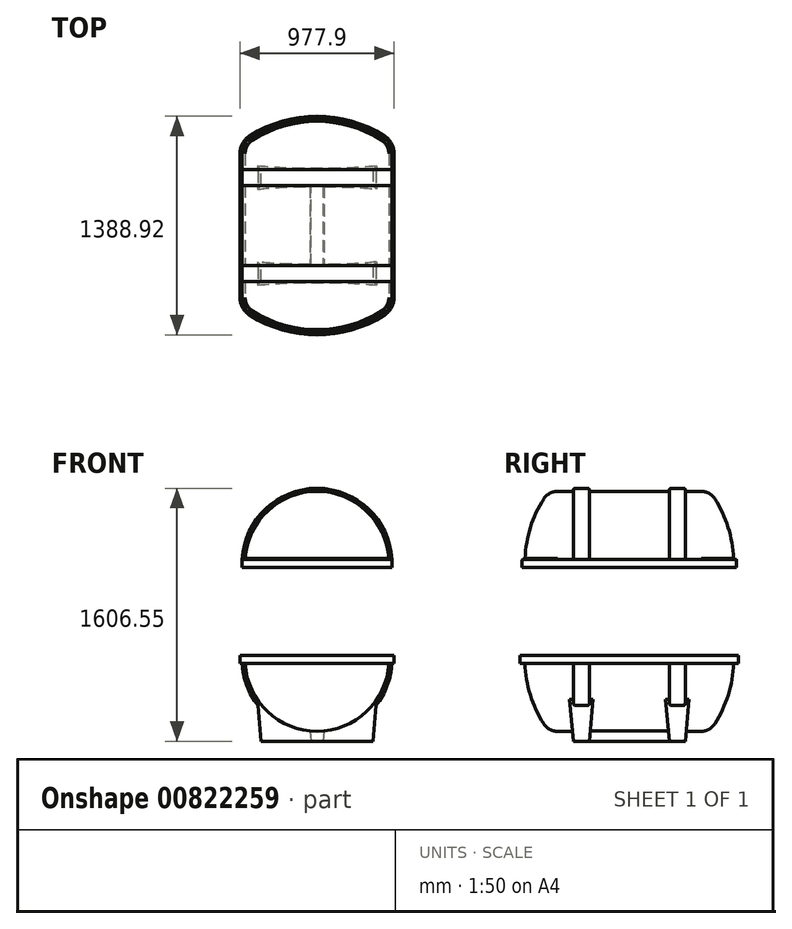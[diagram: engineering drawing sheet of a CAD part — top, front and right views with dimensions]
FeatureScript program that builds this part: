
annotation { "Feature Type Name" : "Feature", "Feature Type Description" : "" }
export const myFeature = defineFeature(function(context is Context, id is Id, definition is map)
    precondition{}
    {
        {
            var Q0;
            Q0=qCreatedBy(makeId("Right.planeOp"),FACE);
            var sketch = newSketch(context, id + "F0", { "sketchPlane" : qUnion([Q0])});
            skLineSegment(sketch, "E0", {"start": v(0, 0) * mm, "end": v(0, 429.3) * mm, "construction": true});
            skLineSegment(sketch, "E1", {"start": v(0, 0) * mm, "end": v(-983.56, 0) * mm, "construction": true});
            skLineSegment(sketch, "E2", {"start": v(0, 457.2) * mm, "end": v(-457.2, 457.2) * mm});
            skArc(sketch, "E3", {"start": v(-457.2, 457.2) * mm, "mid": v(-506, 444.7) * mm, "end": v(-542.81, 410.3) * mm});
            skArc(sketch, "E4", {"start": v(-542.81, 410.3) * mm, "mid": v(-632.12, 213.73) * mm, "end": v(-662.71, 0) * mm});
            skLineSegment(sketch, "E5", {"start": v(-662.71, 0) * mm, "end": v(-662.71, 430.73) * mm, "construction": true});
            skLineSegment(sketch, "E6.MirrorCS", {"start": v(0, 457.2) * mm, "end": v(457.2, 457.2) * mm});
            skArc(sketch, "E7.MirrorCS", {"start": v(457.2, 457.2) * mm, "mid": v(506, 444.7) * mm, "end": v(542.81, 410.3) * mm});
            skArc(sketch, "E8.MirrorCS", {"start": v(542.81, 410.3) * mm, "mid": v(632.12, 213.73) * mm, "end": v(662.71, 0) * mm});
            skLineSegment(sketch, "E9", {"start": v(-662.71, 0) * mm, "end": v(662.71, 0) * mm});
            skLineSegment(sketch, "E10.bottom", {"start": v(254, 457.2) * mm, "end": v(355.6, 457.2) * mm});
            skLineSegment(sketch, "E10.top", {"start": v(263.53, 476.25) * mm, "end": v(346.08, 476.25) * mm});
            skLineSegment(sketch, "E10.left", {"start": v(254, 457.2) * mm, "end": v(254, 466.73) * mm});
            skLineSegment(sketch, "E10.right", {"start": v(355.6, 457.2) * mm, "end": v(355.6, 466.73) * mm});
            skPoint(sketch, "E11.visualSharp", {"position": v(254, 476.25) * mm});
            skArc(sketch, "E11.filletArc", {"start": v(263.53, 476.25) * mm, "mid": v(256.79, 473.46) * mm, "end": v(254, 466.73) * mm});
            skPoint(sketch, "E12.visualSharp", {"position": v(355.6, 476.25) * mm});
            skArc(sketch, "E12.filletArc", {"start": v(355.6, 466.73) * mm, "mid": v(352.81, 473.46) * mm, "end": v(346.08, 476.25) * mm});
            skLineSegment(sketch, "E13.MirrorCS", {"start": v(-355.6, 457.2) * mm, "end": v(-355.6, 466.73) * mm});
            skArc(sketch, "E14.MirrorCS", {"start": v(-263.53, 476.25) * mm, "mid": v(-256.79, 473.46) * mm, "end": v(-254, 466.73) * mm});
            skLineSegment(sketch, "E15.MirrorCS", {"start": v(-254, 457.2) * mm, "end": v(-254, 466.73) * mm});
            skArc(sketch, "E16.MirrorCS", {"start": v(-355.6, 466.73) * mm, "mid": v(-352.81, 473.46) * mm, "end": v(-346.08, 476.25) * mm});
            skPoint(sketch, "E17.MirrorP", {"position": v(-254, 476.25) * mm});
            skLineSegment(sketch, "E18.MirrorCS", {"start": v(-263.53, 476.25) * mm, "end": v(-346.08, 476.25) * mm});
            skLineSegment(sketch, "E19.MirrorCS", {"start": v(-254, 457.2) * mm, "end": v(-355.6, 457.2) * mm});
            skPoint(sketch, "E20.MirrorP", {"position": v(-355.6, 476.25) * mm});
            skSolve(sketch);
        }
        {
            var Q0;
            {var subQ8=sQuery(id+"F0.wireOp",EDGE,"E3");Q0=makeQuery(id+"F0.imprint","IMPRINT",FACE,{"disambiguationData":[TD([[makeQuery(id+"F0.imprint","IMPRINT",EDGE,{"derivedFrom":subQ8}),1.0]])]});}
            var Q1;
            {var subQ1=sQuery(id+"F0.wireOp",EDGE,"E13.MirrorCS");Q1=makeQuery(id+"F0.imprint","IMPRINT",FACE,{"disambiguationData":[TD([[makeQuery(id+"F0.imprint","IMPRINT",EDGE,{"derivedFrom":subQ1}),-1.0]])]});}
            var Q2;
            Q2=makeQuery(id+"F0.imprint","IMPRINT",FACE,{"disambiguationData":[TD([[makeQuery(id+"F0.imprint","IMPRINT",EDGE,{"derivedFrom":sQuery(id+"F0.wireOp",EDGE,"E10.top")}),-1.0]])]});
            var Q3;
            Q3=sQuery(id+"F0.wireOp",EDGE,"E9");
            revolve(context, id + "F1", {"surfaceOperationType" : NewSurfaceOperationType.NEW, "entities" : qUnion([Q0, Q1, Q2]), "axis" : qUnion([Q3]), "revolveType" : RevolveType.SYMMETRIC, "angle" : 180 * degree});
        }
        {
            var Q0;
            Q0=qCreatedBy(makeId("Top.planeOp"),FACE);
            var sketch = newSketch(context, id + "F2", { "sketchPlane" : qUnion([Q0])});
            skArc(sketch, "E21.0", {"start": v(410.3, 542.81) * mm, "mid": v(0, 662.71) * mm, "end": v(-410.3, 542.81) * mm});
            skLineSegment(sketch, "E22.0", {"start": v(-488.95, -457.2) * mm, "end": v(-488.95, 457.2) * mm});
            skArc(sketch, "E22.1", {"start": v(-488.95, -457.2) * mm, "mid": v(-472.56, -521.26) * mm, "end": v(-427.4, -569.57) * mm});
            skArc(sketch, "E22.2", {"start": v(-488.95, 457.2) * mm, "mid": v(-472.56, 521.26) * mm, "end": v(-427.4, 569.57) * mm});
            skArc(sketch, "E22.3", {"start": v(427.4, -569.57) * mm, "mid": v(0, -694.46) * mm, "end": v(-427.4, -569.57) * mm});
            skArc(sketch, "E22.4", {"start": v(427.4, 569.57) * mm, "mid": v(0, 694.46) * mm, "end": v(-427.4, 569.57) * mm});
            skArc(sketch, "E22.5", {"start": v(488.95, 457.2) * mm, "mid": v(472.56, 521.26) * mm, "end": v(427.4, 569.57) * mm});
            skLineSegment(sketch, "E22.6", {"start": v(488.95, -457.2) * mm, "end": v(488.95, 457.2) * mm});
            skArc(sketch, "E22.7", {"start": v(488.95, -457.2) * mm, "mid": v(472.56, -521.26) * mm, "end": v(427.4, -569.57) * mm});
            skSolve(sketch);
        }
        {
            var Q0;
            Q0=makeQuery(id+"F2.imprint","IMPRINT",FACE,{"disambiguationData":[TD([[makeQuery(id+"F2.imprint","IMPRINT",EDGE,{"derivedFrom":sQuery(id+"F2.wireOp",EDGE,"E22.0")}),-1.0]])]});
            extrude(context, id + "F3", {"entities" : qUnion([Q0]), "operationType" : NewBodyOperationType.ADD, "endBound" : BoundingType.SYMMETRIC, "depth" : 50.8 * mm, "offsetDistance" : 25.4 * mm});
        }
        {
            var Q0;
            Q0=qCreatedBy(makeId("Top.planeOp"),FACE);
            cPlane(context, id + "F4", {"entities" : qUnion([Q0]), "cplaneType" : CPlaneType.OFFSET, "offset" : 304.8 * mm, "oppositeDirection" : true, "width" : 152.4 * mm, "height" : 152.4 * mm});
        }
        {
            var Q0;
            Q0=makeQuery(id+"F1.opRevolve","SWEPT_BODY",BODY,{"disambiguationData":[OSD([sQuery(id+"F0.wireOp",EDGE,"E2"),sQuery(id+"F0.wireOp",EDGE,"E3"),sQuery(id+"F0.wireOp",EDGE,"E4"),sQuery(id+"F0.wireOp",EDGE,"E6.MirrorCS"),sQuery(id+"F0.wireOp",EDGE,"E7.MirrorCS"),sQuery(id+"F0.wireOp",EDGE,"E8.MirrorCS"),sQuery(id+"F0.wireOp",EDGE,"E9"),sQuery(id+"F0.wireOp",EDGE,"E10.top"),sQuery(id+"F0.wireOp",EDGE,"E10.left"),sQuery(id+"F0.wireOp",EDGE,"E10.right"),sQuery(id+"F0.wireOp",EDGE,"E11.filletArc"),sQuery(id+"F0.wireOp",EDGE,"E12.filletArc"),sQuery(id+"F0.wireOp",EDGE,"E13.MirrorCS"),sQuery(id+"F0.wireOp",EDGE,"E14.MirrorCS"),sQuery(id+"F0.wireOp",EDGE,"E15.MirrorCS"),sQuery(id+"F0.wireOp",EDGE,"E16.MirrorCS"),sQuery(id+"F0.wireOp",EDGE,"E18.MirrorCS")])]});
            var Q1;
            Q1=qCreatedBy(id+"F4.planeOp",FACE);
            mirror(context, id + "F5", {"entities" : qUnion([Q0]), "mirrorPlane" : qUnion([Q1])});
        }
        {
            var Q0;
            Q0=makeQuery(id+"F3.opExtrude","CAP_FACE",FACE,{"disambiguationData":[OSD([sQuery(id+"F2.wireOp",EDGE,"E22.0"),sQuery(id+"F2.wireOp",EDGE,"E22.1"),sQuery(id+"F2.wireOp",EDGE,"E22.2"),sQuery(id+"F2.wireOp",EDGE,"E22.3"),sQuery(id+"F2.wireOp",EDGE,"E22.4"),sQuery(id+"F2.wireOp",EDGE,"E22.5"),sQuery(id+"F2.wireOp",EDGE,"E22.6"),sQuery(id+"F2.wireOp",EDGE,"E22.7")])],"isStart":true});
            var sketch = newSketch(context, id + "F6", { "sketchPlane" : qUnion([Q0])});
            skLineSegment(sketch, "E23.0", {"start": v(476.25, -457.2) * mm, "end": v(476.25, 457.2) * mm});
            skArc(sketch, "E23.1", {"start": v(420.57, -558.87) * mm, "mid": v(461.42, -515.16) * mm, "end": v(476.25, -457.2) * mm});
            skArc(sketch, "E23.2", {"start": v(476.25, 457.2) * mm, "mid": v(461.42, 515.16) * mm, "end": v(420.57, 558.87) * mm});
            skArc(sketch, "E23.3", {"start": v(-420.57, -558.87) * mm, "mid": v(0, -681.76) * mm, "end": v(420.57, -558.87) * mm});
            skArc(sketch, "E23.4", {"start": v(420.57, 558.87) * mm, "mid": v(0, 681.76) * mm, "end": v(-420.57, 558.87) * mm});
            skArc(sketch, "E23.5", {"start": v(-420.57, 558.87) * mm, "mid": v(-461.42, 515.16) * mm, "end": v(-476.25, 457.2) * mm});
            skLineSegment(sketch, "E23.6", {"start": v(-476.25, 457.2) * mm, "end": v(-476.25, -457.2) * mm});
            skArc(sketch, "E23.7", {"start": v(-476.25, -457.2) * mm, "mid": v(-461.42, -515.16) * mm, "end": v(-420.57, -558.87) * mm});
            skSolve(sketch);
        }
        {
            var Q0;
            Q0=makeQuery(id+"F6.imprint","IMPRINT",FACE,{"disambiguationData":[TD([[makeQuery(id+"F6.imprint","IMPRINT",EDGE,{"derivedFrom":sQuery(id+"F6.wireOp",EDGE,"E23.0")}),-1.0]])]});
            extrude(context, id + "F7", {"entities" : qUnion([Q0]), "operationType" : NewBodyOperationType.REMOVE, "endBound" : BoundingType.THROUGH_ALL, "oppositeDirection" : true, "depth" : 25.4 * mm, "offsetDistance" : 25.4 * mm});
        }
        {
            var Q0;
            Q0=makeQuery(id+"F5.opPattern","COPY",FACE,{"derivedFrom":makeQuery(id+"F3.opExtrude","CAP_FACE",FACE,{"disambiguationData":[OSD([sQuery(id+"F2.wireOp",EDGE,"E22.0"),sQuery(id+"F2.wireOp",EDGE,"E22.1"),sQuery(id+"F2.wireOp",EDGE,"E22.2"),sQuery(id+"F2.wireOp",EDGE,"E22.3"),sQuery(id+"F2.wireOp",EDGE,"E22.4"),sQuery(id+"F2.wireOp",EDGE,"E22.5"),sQuery(id+"F2.wireOp",EDGE,"E22.6"),sQuery(id+"F2.wireOp",EDGE,"E22.7")])],"isStart":true}),"instanceName":"1"});
            cPlane(context, id + "F8", {"entities" : qUnion([Q0]), "cplaneType" : CPlaneType.OFFSET, "offset" : 546.1 * mm, "oppositeDirection" : true, "width" : 152.4 * mm, "height" : 152.4 * mm});
        }
        {
            var Q0;
            Q0=qCreatedBy(id+"F8.planeOp",FACE);
            var sketch = newSketch(context, id + "F9", { "sketchPlane" : qUnion([Q0])});
            skLineSegment(sketch, "E24", {"start": v(0, 0) * mm, "end": v(38.1, 0) * mm});
            skLineSegment(sketch, "E25", {"start": v(38.1, 0) * mm, "end": v(38.1, -254) * mm});
            skLineSegment(sketch, "E26", {"start": v(38.1, -254) * mm, "end": v(355.6, -254) * mm});
            skLineSegment(sketch, "E27", {"start": v(355.6, -254) * mm, "end": v(355.6, -355.6) * mm});
            skLineSegment(sketch, "E28", {"start": v(355.6, -355.6) * mm, "end": v(0, -355.6) * mm});
            skLineSegment(sketch, "E29", {"start": v(0, -355.6) * mm, "end": v(0, 0) * mm, "construction": true});
            skLineSegment(sketch, "E30", {"start": v(414.4, 0) * mm, "end": v(0, 0) * mm, "construction": true});
            skLineSegment(sketch, "E31.MirrorCS", {"start": v(0, 0) * mm, "end": v(-38.1, 0) * mm});
            skLineSegment(sketch, "E32.MirrorCS", {"start": v(-38.1, 0) * mm, "end": v(-38.1, -254) * mm});
            skLineSegment(sketch, "E33.MirrorCS", {"start": v(-38.1, -254) * mm, "end": v(-355.6, -254) * mm});
            skLineSegment(sketch, "E34.MirrorCS", {"start": v(-355.6, -254) * mm, "end": v(-355.6, -355.6) * mm});
            skLineSegment(sketch, "E35.MirrorCS", {"start": v(-355.6, -355.6) * mm, "end": v(0, -355.6) * mm});
            skLineSegment(sketch, "E36.MirrorCS", {"start": v(38.1, 0) * mm, "end": v(38.1, 254) * mm});
            skLineSegment(sketch, "E37.MirrorCS", {"start": v(38.1, 254) * mm, "end": v(355.6, 254) * mm});
            skLineSegment(sketch, "E38.MirrorCS", {"start": v(355.6, 355.6) * mm, "end": v(0, 355.6) * mm});
            skLineSegment(sketch, "E39.MirrorCS", {"start": v(355.6, 254) * mm, "end": v(355.6, 355.6) * mm});
            skLineSegment(sketch, "E40.MirrorCS", {"start": v(-355.6, 254) * mm, "end": v(-355.6, 355.6) * mm});
            skLineSegment(sketch, "E41.MirrorCS", {"start": v(-355.6, 355.6) * mm, "end": v(0, 355.6) * mm});
            skLineSegment(sketch, "E42.MirrorCS", {"start": v(-38.1, 254) * mm, "end": v(-355.6, 254) * mm});
            skLineSegment(sketch, "E43.MirrorCS", {"start": v(-38.1, 0) * mm, "end": v(-38.1, 254) * mm});
            skSolve(sketch);
        }
        {
            var Q0;
            Q0=makeQuery(id+"F9.imprint","IMPRINT",FACE,{"disambiguationData":[TD([[makeQuery(id+"F9.imprint","IMPRINT",EDGE,{"derivedFrom":sQuery(id+"F9.wireOp",EDGE,"E24")}),-1.0]])]});
            var Q1;
            Q1=makeQuery(id+"F9.imprint","IMPRINT",FACE,{"disambiguationData":[TD([[makeQuery(id+"F9.imprint","IMPRINT",EDGE,{"derivedFrom":sQuery(id+"F9.wireOp",EDGE,"E24")}),1.0]])]});
            var Q2;
            Q2=makeQuery(id+"F5.opPattern","COPY",FACE,{"derivedFrom":makeQuery(id+"F1.opRevolve","SWEPT_FACE",FACE,{"disambiguationData":[OSD([sQuery(id+"F0.wireOp",EDGE,"E2"),sQuery(id+"F0.wireOp",EDGE,"E6.MirrorCS")])]}),"instanceName":"1"});
            extrude(context, id + "F10", {"entities" : qUnion([Q0, Q1]), "operationType" : NewBodyOperationType.ADD, "endBound" : BoundingType.UP_TO_SURFACE, "depth" : 25.4 * mm, "endBoundEntityFace" : qUnion([Q2]), "offsetDistance" : 25.4 * mm, "hasDraft" : true, "draftAngle" : 5 * degree});
        }
        {
            var Q0;
            Q0=makeQuery(id+"F7.boolean.opBoolean","INTERSECT",EDGE,{"derivedFrom":[makeQuery(id+"F3.opExtrude","CAP_FACE",FACE,{"disambiguationData":[OSD([sQuery(id+"F2.wireOp",EDGE,"E22.0"),sQuery(id+"F2.wireOp",EDGE,"E22.1"),sQuery(id+"F2.wireOp",EDGE,"E22.2"),sQuery(id+"F2.wireOp",EDGE,"E22.3"),sQuery(id+"F2.wireOp",EDGE,"E22.4"),sQuery(id+"F2.wireOp",EDGE,"E22.5"),sQuery(id+"F2.wireOp",EDGE,"E22.6"),sQuery(id+"F2.wireOp",EDGE,"E22.7")])],"isStart":false}),makeQuery(id+"F7.opExtrude","SWEPT_FACE",FACE,{"disambiguationData":[OSD([sQuery(id+"F6.wireOp",EDGE,"E23.6")])]})]});
            var Q1;
            Q1=makeQuery(id+"F7.boolean.opBoolean","INTERSECT",EDGE,{"derivedFrom":[makeQuery(id+"F3.opExtrude","CAP_FACE",FACE,{"disambiguationData":[OSD([sQuery(id+"F2.wireOp",EDGE,"E22.0"),sQuery(id+"F2.wireOp",EDGE,"E22.1"),sQuery(id+"F2.wireOp",EDGE,"E22.2"),sQuery(id+"F2.wireOp",EDGE,"E22.3"),sQuery(id+"F2.wireOp",EDGE,"E22.4"),sQuery(id+"F2.wireOp",EDGE,"E22.5"),sQuery(id+"F2.wireOp",EDGE,"E22.6"),sQuery(id+"F2.wireOp",EDGE,"E22.7")])],"isStart":false}),makeQuery(id+"F7.opExtrude","SWEPT_FACE",FACE,{"disambiguationData":[OSD([sQuery(id+"F6.wireOp",EDGE,"E23.5")])]})]});
            var Q2;
            Q2=makeQuery(id+"F3.boolean.opBoolean","INTERSECT",EDGE,{"derivedFrom":[makeQuery(id+"F1.opRevolve","SWEPT_FACE",FACE,{"disambiguationData":[OSD([sQuery(id+"F0.wireOp",EDGE,"E4")])]}),makeQuery(id+"F3.opExtrude","CAP_FACE",FACE,{"disambiguationData":[OSD([sQuery(id+"F2.wireOp",EDGE,"E22.0"),sQuery(id+"F2.wireOp",EDGE,"E22.1"),sQuery(id+"F2.wireOp",EDGE,"E22.2"),sQuery(id+"F2.wireOp",EDGE,"E22.3"),sQuery(id+"F2.wireOp",EDGE,"E22.4"),sQuery(id+"F2.wireOp",EDGE,"E22.5"),sQuery(id+"F2.wireOp",EDGE,"E22.6"),sQuery(id+"F2.wireOp",EDGE,"E22.7")])],"isStart":false})]});
            var Q3;
            Q3=makeQuery(id+"F3.boolean.opBoolean","INTERSECT",EDGE,{"disambiguationData":[OD(0.0)],"derivedFrom":[makeQuery(id+"F1.opRevolve","SWEPT_FACE",FACE,{"disambiguationData":[OSD([sQuery(id+"F0.wireOp",EDGE,"E2"),sQuery(id+"F0.wireOp",EDGE,"E6.MirrorCS")])]}),makeQuery(id+"F3.opExtrude","CAP_FACE",FACE,{"disambiguationData":[OSD([sQuery(id+"F2.wireOp",EDGE,"E22.0"),sQuery(id+"F2.wireOp",EDGE,"E22.1"),sQuery(id+"F2.wireOp",EDGE,"E22.2"),sQuery(id+"F2.wireOp",EDGE,"E22.3"),sQuery(id+"F2.wireOp",EDGE,"E22.4"),sQuery(id+"F2.wireOp",EDGE,"E22.5"),sQuery(id+"F2.wireOp",EDGE,"E22.6"),sQuery(id+"F2.wireOp",EDGE,"E22.7")])],"isStart":false})]});
            var Q4;
            Q4=makeQuery(id+"F3.boolean.opBoolean","INTERSECT",EDGE,{"disambiguationData":[OD(0.0)],"derivedFrom":[makeQuery(id+"F1.opRevolve","SWEPT_FACE",FACE,{"disambiguationData":[OSD([sQuery(id+"F0.wireOp",EDGE,"E7.MirrorCS")])]}),makeQuery(id+"F3.opExtrude","CAP_FACE",FACE,{"disambiguationData":[OSD([sQuery(id+"F2.wireOp",EDGE,"E22.0"),sQuery(id+"F2.wireOp",EDGE,"E22.1"),sQuery(id+"F2.wireOp",EDGE,"E22.2"),sQuery(id+"F2.wireOp",EDGE,"E22.3"),sQuery(id+"F2.wireOp",EDGE,"E22.4"),sQuery(id+"F2.wireOp",EDGE,"E22.5"),sQuery(id+"F2.wireOp",EDGE,"E22.6"),sQuery(id+"F2.wireOp",EDGE,"E22.7")])],"isStart":false})]});
            var Q5;
            Q5=makeQuery(id+"F1.opRevolve","SWEPT_EDGE",EDGE,{"disambiguationData":[OSD([sQuery(id+"F0.wireOp",EDGE,"E6.MirrorCS"),sQuery(id+"F0.wireOp",EDGE,"E10.left")])]});
            var Q6;
            Q6=makeQuery(id+"F1.opRevolve","SWEPT_EDGE",EDGE,{"disambiguationData":[OSD([sQuery(id+"F0.wireOp",EDGE,"E6.MirrorCS"),sQuery(id+"F0.wireOp",EDGE,"E10.right")])]});
            var Q7;
            Q7=makeQuery(id+"F1.opRevolve","SWEPT_EDGE",EDGE,{"disambiguationData":[OSD([sQuery(id+"F0.wireOp",EDGE,"E2"),sQuery(id+"F0.wireOp",EDGE,"E15.MirrorCS")])]});
            var Q8;
            Q8=makeQuery(id+"F1.opRevolve","SWEPT_EDGE",EDGE,{"disambiguationData":[OSD([sQuery(id+"F0.wireOp",EDGE,"E2"),sQuery(id+"F0.wireOp",EDGE,"E13.MirrorCS")])]});
            var Q9;
            Q9=makeQuery(id+"F3.boolean.opBoolean","INTERSECT",EDGE,{"disambiguationData":[OD(1.0)],"derivedFrom":[makeQuery(id+"F1.opRevolve","SWEPT_FACE",FACE,{"disambiguationData":[OSD([sQuery(id+"F0.wireOp",EDGE,"E2"),sQuery(id+"F0.wireOp",EDGE,"E6.MirrorCS")])]}),makeQuery(id+"F3.opExtrude","CAP_FACE",FACE,{"disambiguationData":[OSD([sQuery(id+"F2.wireOp",EDGE,"E22.0"),sQuery(id+"F2.wireOp",EDGE,"E22.1"),sQuery(id+"F2.wireOp",EDGE,"E22.2"),sQuery(id+"F2.wireOp",EDGE,"E22.3"),sQuery(id+"F2.wireOp",EDGE,"E22.4"),sQuery(id+"F2.wireOp",EDGE,"E22.5"),sQuery(id+"F2.wireOp",EDGE,"E22.6"),sQuery(id+"F2.wireOp",EDGE,"E22.7")])],"isStart":false})]});
            fillet(context, id + "F11", {"entities" : qUnion([Q0, Q1, Q2, Q3, Q4, Q5, Q6, Q7, Q8, Q9]), "radius" : 6.35 * mm, "tangentPropagation" : true, "allowEdgeOverflow" : false});
        }
    });
